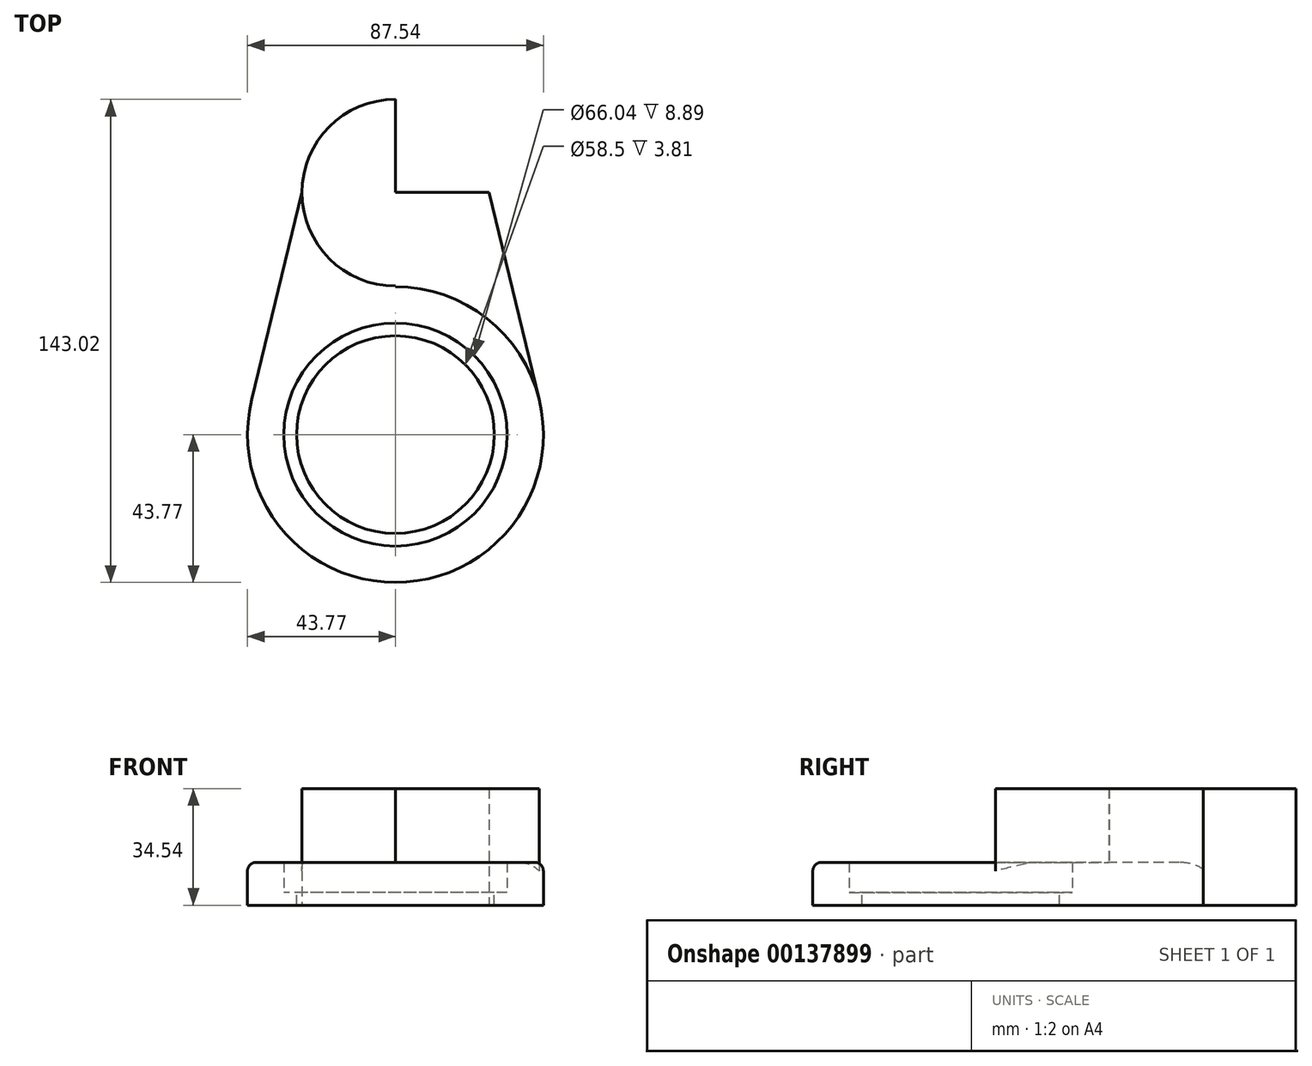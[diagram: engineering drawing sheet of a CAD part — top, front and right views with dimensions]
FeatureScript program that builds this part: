
annotation { "Feature Type Name" : "Feature", "Feature Type Description" : "" }
export const myFeature = defineFeature(function(context is Context, id is Id, definition is map)
    precondition{}
    {
        {
            var Q0;
            Q0=qCreatedBy(makeId("Top.planeOp"),FACE);
            var sketch = newSketch(context, id + "F0", { "sketchPlane" : qUnion([Q0])});
            skCircle(sketch, "E0", {"center": v(0, 0) * mm, "radius": 33.02 * mm});
            skCircle(sketch, "E1", {"center": v(0, 0) * mm, "radius": 43.77 * mm});
            skLineSegment(sketch, "E2", {"start": v(0, 0) * mm, "end": v(0, 110.9) * mm});
            skCircle(sketch, "E3", {"center": v(0, 71.61) * mm, "radius": 27.63 * mm});
            skLineSegment(sketch, "E4", {"start": v(-27.63, 71.76) * mm, "end": v(-42.53, 10.31) * mm});
            skLineSegment(sketch, "E5", {"start": v(-27.63, 71.76) * mm, "end": v(27.63, 71.76) * mm});
            skLineSegment(sketch, "E6", {"start": v(27.63, 71.76) * mm, "end": v(42.53, 10.31) * mm});
            skLineSegment(sketch, "E7", {"start": v(153.23, -43.77) * mm, "end": v(153.23, 110.9) * mm});
            skSolve(sketch);
        }
        {
            var Q0;
            Q0=makeQuery(id+"F0.imprint","IMPRINT",FACE,{"disambiguationData":[TD([[makeQuery(id+"F0.imprint","IMPRINT",EDGE,{"derivedFrom":sQuery(id+"F0.wireOp",EDGE,"E0")}),1.0]])]});
            extrude(context, id + "F1", {"entities" : qUnion([Q0]), "depth" : 3.8 * mm});
        }
        {
            var Q0;
            Q0=makeQuery(id+"F0.imprint","IMPRINT",FACE,{"disambiguationData":[TD([[makeQuery(id+"F0.imprint","IMPRINT",EDGE,{"derivedFrom":sQuery(id+"F0.wireOp",EDGE,"E0")}),-1.0]])]});
            extrude(context, id + "F2", {"entities" : qUnion([Q0]), "operationType" : NewBodyOperationType.ADD, "depth" : 12.7 * mm});
        }
        {
            var Q0;
            {var subQ0=sQuery(id+"F0.wireOp",EDGE,"E4");Q0=makeQuery(id+"F0.imprint","IMPRINT",FACE,{"disambiguationData":[TD([[makeQuery(id+"F0.imprint","IMPRINT",EDGE,{"derivedFrom":subQ0}),1.0]])]});}
            var Q1;
            {var subQ0=sQuery(id+"F0.wireOp",EDGE,"E6");Q1=makeQuery(id+"F0.imprint","IMPRINT",FACE,{"disambiguationData":[TD([[makeQuery(id+"F0.imprint","IMPRINT",EDGE,{"derivedFrom":subQ0}),-1.0]])]});}
            extrude(context, id + "F3", {"entities" : qUnion([Q0, Q1]), "operationType" : NewBodyOperationType.ADD, "depth" : 12.7 * mm});
        }
        {
            var Q0;
            {var subQ0=sQuery(id+"F0.wireOp",EDGE,"E5");var subQ4=makeQuery(id+"F0.imprint","INTERSECT",VERTEX,{"derivedFrom":[sQuery(id+"F0.wireOp",EDGE,"E2"),subQ0]});Q0=makeQuery(id+"F0.imprint","IMPRINT",FACE,{"disambiguationData":[TD([[makeQuery(id+"F0.imprint","IMPRINT",EDGE,{"disambiguationData":[TD([[subQ4,1.0]])],"derivedFrom":subQ0}),1.0]])]});}
            var Q1;
            {var subQ0=sQuery(id+"F0.wireOp",EDGE,"E5");var subQ1=sQuery(id+"F0.wireOp",EDGE,"E2");var subQ2=makeQuery(id+"F0.imprint","INTERSECT",VERTEX,{"derivedFrom":[subQ1,subQ0]});Q1=makeQuery(id+"F0.imprint","IMPRINT",FACE,{"disambiguationData":[TD([[makeQuery(id+"F0.imprint","IMPRINT",EDGE,{"disambiguationData":[TD([[subQ2,1.0]])],"derivedFrom":subQ1}),-1.0]])]});}
            var Q2;
            {var subQ0=sQuery(id+"F0.wireOp",EDGE,"E5");var subQ1=sQuery(id+"F0.wireOp",EDGE,"E2");var subQ2=makeQuery(id+"F0.imprint","INTERSECT",VERTEX,{"derivedFrom":[subQ1,subQ0]});Q2=makeQuery(id+"F0.imprint","IMPRINT",FACE,{"disambiguationData":[TD([[makeQuery(id+"F0.imprint","IMPRINT",EDGE,{"disambiguationData":[TD([[subQ2,1.0]])],"derivedFrom":subQ1}),1.0]])]});}
            var Q3;
            {var subQ0=sQuery(id+"F0.wireOp",EDGE,"E3");var subQ1=sQuery(id+"F0.wireOp",EDGE,"E2");var subQ2=makeQuery(id+"F0.imprint","INTERSECT",VERTEX,{"disambiguationData":[OD(0.0)],"derivedFrom":[subQ1,subQ0]});Q3=makeQuery(id+"F0.imprint","IMPRINT",FACE,{"disambiguationData":[TD([[makeQuery(id+"F0.imprint","IMPRINT",EDGE,{"disambiguationData":[TD([[subQ2,1.0]])],"derivedFrom":subQ1}),-1.0]])]});}
            extrude(context, id + "F4", {"entities" : qUnion([Q0, Q1, Q2, Q3]), "operationType" : NewBodyOperationType.ADD, "depth" : 34.54 * mm});
        }
        {
            var Q0;
            Q0=makeQuery(id+"F1.opExtrude","CAP_FACE",FACE,{"disambiguationData":[OSD([sQuery(id+"F0.wireOp",EDGE,"E0")])],"isStart":false});
            var sketch = newSketch(context, id + "F5", { "sketchPlane" : qUnion([Q0])});
            skCircle(sketch, "E8", {"center": v(0, 0) * mm, "radius": 29.25 * mm});
            skSolve(sketch);
        }
        {
            var Q0;
            Q0=makeQuery(id+"F5.imprint","IMPRINT",FACE,{"disambiguationData":[TD([[makeQuery(id+"F5.imprint","IMPRINT",EDGE,{"derivedFrom":sQuery(id+"F5.wireOp",EDGE,"E8")}),1.0]])]});
            extrude(context, id + "F6", {"entities" : qUnion([Q0]), "operationType" : NewBodyOperationType.REMOVE, "oppositeDirection" : true, "depth" : 25.4 * mm});
        }
        {
            var Q0;
            Q0=makeQuery(id+"F3.opExtrude","CAP_EDGE",EDGE,{"disambiguationData":[OSD([sQuery(id+"F0.wireOp",EDGE,"E6")])],"isStart":false});
            var Q1;
            Q1=makeQuery(id+"F2.opExtrude","CAP_EDGE",EDGE,{"disambiguationData":[OSD([sQuery(id+"F0.wireOp",EDGE,"E1")])],"isStart":false});
            var Q2;
            Q2=makeQuery(id+"F3.opExtrude","CAP_EDGE",EDGE,{"disambiguationData":[OSD([sQuery(id+"F0.wireOp",EDGE,"E4")])],"isStart":false});
            fillet(context, id + "F7", {"entities" : qUnion([Q0, Q1, Q2]), "radius" : 2.54 * mm, "tangentPropagation" : true, "allowEdgeOverflow" : false});
        }
    });
